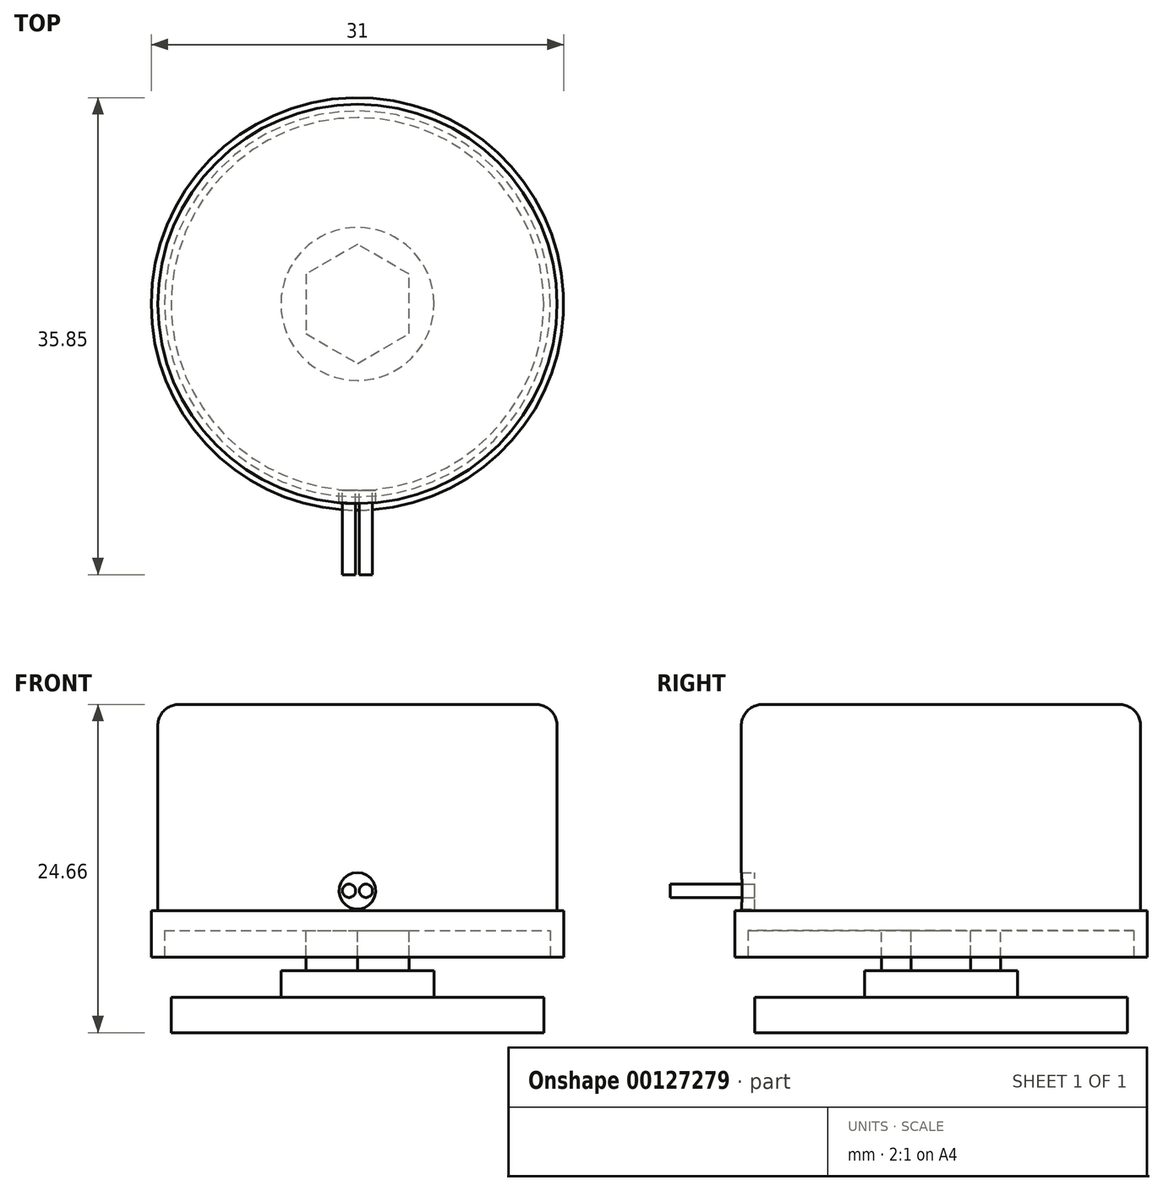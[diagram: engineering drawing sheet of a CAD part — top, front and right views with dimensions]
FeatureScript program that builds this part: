
annotation { "Feature Type Name" : "Feature", "Feature Type Description" : "" }
export const myFeature = defineFeature(function(context is Context, id is Id, definition is map)
    precondition{}
    {
        {
            var Q0;
            Q0=qCreatedBy(makeId("Top.planeOp"),FACE);
            var sketch = newSketch(context, id + "F0", { "sketchPlane" : qUnion([Q0])});
            skCircle(sketch, "E0", {"center": v(0, 0) * mm, "radius": 15 * mm});
            skSolve(sketch);
        }
        {
            var Q0;
            Q0=qSketchRegion(id+"F0",true);
            extrude(context, id + "F1", {"entities" : qUnion([Q0]), "depth" : 19 * mm});
        }
        {
            var Q0;
            Q0=makeQuery(id+"F1.opExtrude","CAP_EDGE",EDGE,{"disambiguationData":[OSD([sQuery(id+"F0.wireOp",EDGE,"E0")])],"isStart":false});
            fillet(context, id + "F2", {"entities" : qUnion([Q0]), "radius" : 1.59 * mm, "tangentPropagation" : true, "allowEdgeOverflow" : false});
        }
        {
            var Q0;
            Q0=makeQuery(id+"F1.opExtrude","CAP_FACE",FACE,{"disambiguationData":[OSD([sQuery(id+"F0.wireOp",EDGE,"E0")])],"isStart":true});
            var sketch = newSketch(context, id + "F3", { "sketchPlane" : qUnion([Q0])});
            skCircle(sketch, "E1", {"center": v(0, 0) * mm, "radius": 15.5 * mm});
            skSolve(sketch);
        }
        {
            var Q0;
            Q0=makeQuery(id+"F3.imprint","IMPRINT",FACE,{"disambiguationData":[TD([[makeQuery(id+"F3.imprint","IMPRINT",EDGE,{"derivedFrom":sQuery(id+"F3.wireOp",EDGE,"E1")}),1.0]])]});
            extrude(context, id + "F4", {"entities" : qUnion([Q0]), "operationType" : NewBodyOperationType.ADD, "oppositeDirection" : true, "depth" : 3.5 * mm});
        }
        {
            var Q0;
            {var subQ0=sQuery(id+"F0.wireOp",EDGE,"E0");Q0=makeQuery(id+"F4.boolean.opBoolean","MERGE",FACE,{"derivedFrom":[makeQuery(id+"F1.opExtrude","CAP_FACE",FACE,{"disambiguationData":[OSD([subQ0])],"isStart":true}),makeQuery(id+"F4.opExtrude","CAP_FACE",FACE,{"disambiguationData":[OSD([subQ0,sQuery(id+"F3.wireOp",EDGE,"E1")])],"isStart":true})]});}
            var sketch = newSketch(context, id + "F5", { "sketchPlane" : qUnion([Q0])});
            skCircle(sketch, "E2", {"center": v(0, 0) * mm, "radius": 14.5 * mm});
            skSolve(sketch);
        }
        {
            var Q0;
            Q0=makeQuery(id+"F5.imprint","IMPRINT",FACE,{"disambiguationData":[TD([[makeQuery(id+"F5.imprint","IMPRINT",EDGE,{"derivedFrom":sQuery(id+"F5.wireOp",EDGE,"E2")}),1.0]])]});
            extrude(context, id + "F6", {"entities" : qUnion([Q0]), "operationType" : NewBodyOperationType.REMOVE, "oppositeDirection" : true, "depth" : 2 * mm});
        }
        {
            var Q0;
            Q0=makeQuery(id+"F6.boolean.opBoolean","COPY",FACE,{"derivedFrom":makeQuery(id+"F6.opExtrude","CAP_FACE",FACE,{"disambiguationData":[OSD([sQuery(id+"F5.wireOp",EDGE,"E2")])],"isStart":false})});
            var sketch = newSketch(context, id + "F7", { "sketchPlane" : qUnion([Q0])});
            skCircle(sketch, "E3.cCircle", {"center": v(0, 0) * mm, "radius": 3.88 * mm, "construction": true});
            skLineSegment(sketch, "E3.0", {"start": v(-3.87, 2.24) * mm, "end": v(0, 4.47) * mm});
            skLineSegment(sketch, "E3.1", {"start": v(0, 4.47) * mm, "end": v(3.88, 2.24) * mm});
            skLineSegment(sketch, "E3.2", {"start": v(3.88, 2.24) * mm, "end": v(3.88, -2.24) * mm});
            skLineSegment(sketch, "E3.3", {"start": v(3.88, -2.24) * mm, "end": v(0, -4.47) * mm});
            skLineSegment(sketch, "E3.4", {"start": v(0, -4.47) * mm, "end": v(-3.88, -2.24) * mm});
            skLineSegment(sketch, "E3.5", {"start": v(-3.88, -2.24) * mm, "end": v(-3.87, 2.24) * mm});
            skPoint(sketch, "E3.0.midPoint", {"position": v(-1.94, 3.36) * mm});
            skSolve(sketch);
        }
        {
            var Q0;
            Q0=makeQuery(id+"F7.imprint","IMPRINT",FACE,{"disambiguationData":[TD([[makeQuery(id+"F7.imprint","IMPRINT",EDGE,{"derivedFrom":sQuery(id+"F7.wireOp",EDGE,"E3.0")}),-1.0]])]});
            extrude(context, id + "F8", {"entities" : qUnion([Q0]), "operationType" : NewBodyOperationType.ADD, "depth" : 3 * mm});
        }
        {
            var Q0;
            Q0=makeQuery(id+"F8.opExtrude","CAP_FACE",FACE,{"disambiguationData":[OSD([sQuery(id+"F7.wireOp",EDGE,"E3.0"),sQuery(id+"F7.wireOp",EDGE,"E3.1"),sQuery(id+"F7.wireOp",EDGE,"E3.2"),sQuery(id+"F7.wireOp",EDGE,"E3.3"),sQuery(id+"F7.wireOp",EDGE,"E3.4"),sQuery(id+"F7.wireOp",EDGE,"E3.5")])],"isStart":false});
            var sketch = newSketch(context, id + "F9", { "sketchPlane" : qUnion([Q0])});
            skCircle(sketch, "E4", {"center": v(0, 0) * mm, "radius": 5.75 * mm});
            skSolve(sketch);
        }
        {
            var Q0;
            Q0=makeQuery(id+"F9.imprint","IMPRINT",FACE,{"disambiguationData":[TD([[makeQuery(id+"F9.imprint","IMPRINT",EDGE,{"derivedFrom":makeQuery(id+"F8.opExtrude","CAP_EDGE",EDGE,{"disambiguationData":[OSD([sQuery(id+"F7.wireOp",EDGE,"E3.0")])],"isStart":false})}),-1.0]])]});
            var Q1;
            Q1=makeQuery(id+"F9.imprint","IMPRINT",FACE,{"disambiguationData":[TD([[makeQuery(id+"F9.imprint","IMPRINT",EDGE,{"derivedFrom":sQuery(id+"F9.wireOp",EDGE,"E4")}),1.0]])]});
            extrude(context, id + "F10", {"entities" : qUnion([Q0, Q1]), "operationType" : NewBodyOperationType.ADD, "depth" : 2 * mm});
        }
        {
            var Q0;
            Q0=makeQuery(id+"F10.opExtrude","CAP_FACE",FACE,{"disambiguationData":[OSD([sQuery(id+"F9.wireOp",EDGE,"E4")])],"isStart":false});
            var sketch = newSketch(context, id + "F11", { "sketchPlane" : qUnion([Q0])});
            skCircle(sketch, "E5", {"center": v(0, 0) * mm, "radius": 14 * mm});
            skSolve(sketch);
        }
        {
            var Q0;
            Q0=makeQuery(id+"F11.imprint","IMPRINT",FACE,{"disambiguationData":[TD([[makeQuery(id+"F11.imprint","IMPRINT",EDGE,{"derivedFrom":sQuery(id+"F11.wireOp",EDGE,"E5")}),1.0]])]});
            var Q1;
            Q1=makeQuery(id+"F11.imprint","IMPRINT",FACE,{"disambiguationData":[TD([[makeQuery(id+"F11.imprint","IMPRINT",EDGE,{"derivedFrom":makeQuery(id+"F10.opExtrude","CAP_EDGE",EDGE,{"disambiguationData":[OSD([sQuery(id+"F9.wireOp",EDGE,"E4")])],"isStart":false})}),1.0]])]});
            extrude(context, id + "F12", {"entities" : qUnion([Q0, Q1]), "operationType" : NewBodyOperationType.ADD, "depth" : 2.66 * mm});
        }
        {
            var Q0;
            Q0=qCreatedBy(makeId("Front.planeOp"),FACE);
            var sketch = newSketch(context, id + "F13", { "sketchPlane" : qUnion([Q0])});
            skCircle(sketch, "E6", {"center": v(0, 5) * mm, "radius": 1.38 * mm});
            skSolve(sketch);
        }
        {
            var Q0;
            Q0=qSketchRegion(id+"F13",true);
            extrude(context, id + "F14", {"entities" : qUnion([Q0]), "operationType" : NewBodyOperationType.REMOVE, "depth" : 25.4 * mm, "hasSecondDirection" : true, "secondDirectionOppositeDirection" : false, "secondDirectionDepth" : 14 * mm});
        }
        {
            var Q0;
            Q0=makeQuery(id+"F14.boolean.opBoolean","COPY",FACE,{"derivedFrom":makeQuery(id+"F14.opExtrude","CAP_FACE",FACE,{"disambiguationData":[OSD([sQuery(id+"F13.wireOp",EDGE,"E6")])],"isStart":true})});
            var sketch = newSketch(context, id + "F15", { "sketchPlane" : qUnion([Q0])});
            skCircle(sketch, "E7", {"center": v(-0.64, 5) * mm, "radius": 0.5 * mm});
            skCircle(sketch, "E8", {"center": v(0.63, 5) * mm, "radius": 0.5 * mm});
            skCircle(sketch, "E9.0", {"center": v(0, 5) * mm, "radius": 1.38 * mm});
            skLineSegment(sketch, "E10", {"start": v(-0.64, 5) * mm, "end": v(0.63, 5) * mm, "construction": true});
            skSolve(sketch);
        }
        {
            var Q0;
            Q0=makeQuery(id+"F15.imprint","IMPRINT",FACE,{"disambiguationData":[TD([[makeQuery(id+"F15.imprint","IMPRINT",EDGE,{"derivedFrom":sQuery(id+"F15.wireOp",EDGE,"E7")}),1.0]])]});
            var Q1;
            Q1=makeQuery(id+"F15.imprint","IMPRINT",FACE,{"disambiguationData":[TD([[makeQuery(id+"F15.imprint","IMPRINT",EDGE,{"derivedFrom":sQuery(id+"F15.wireOp",EDGE,"E8")}),1.0]])]});
            extrude(context, id + "F16", {"entities" : qUnion([Q0, Q1]), "operationType" : NewBodyOperationType.ADD, "depth" : 6.35 * mm});
        }
    });
